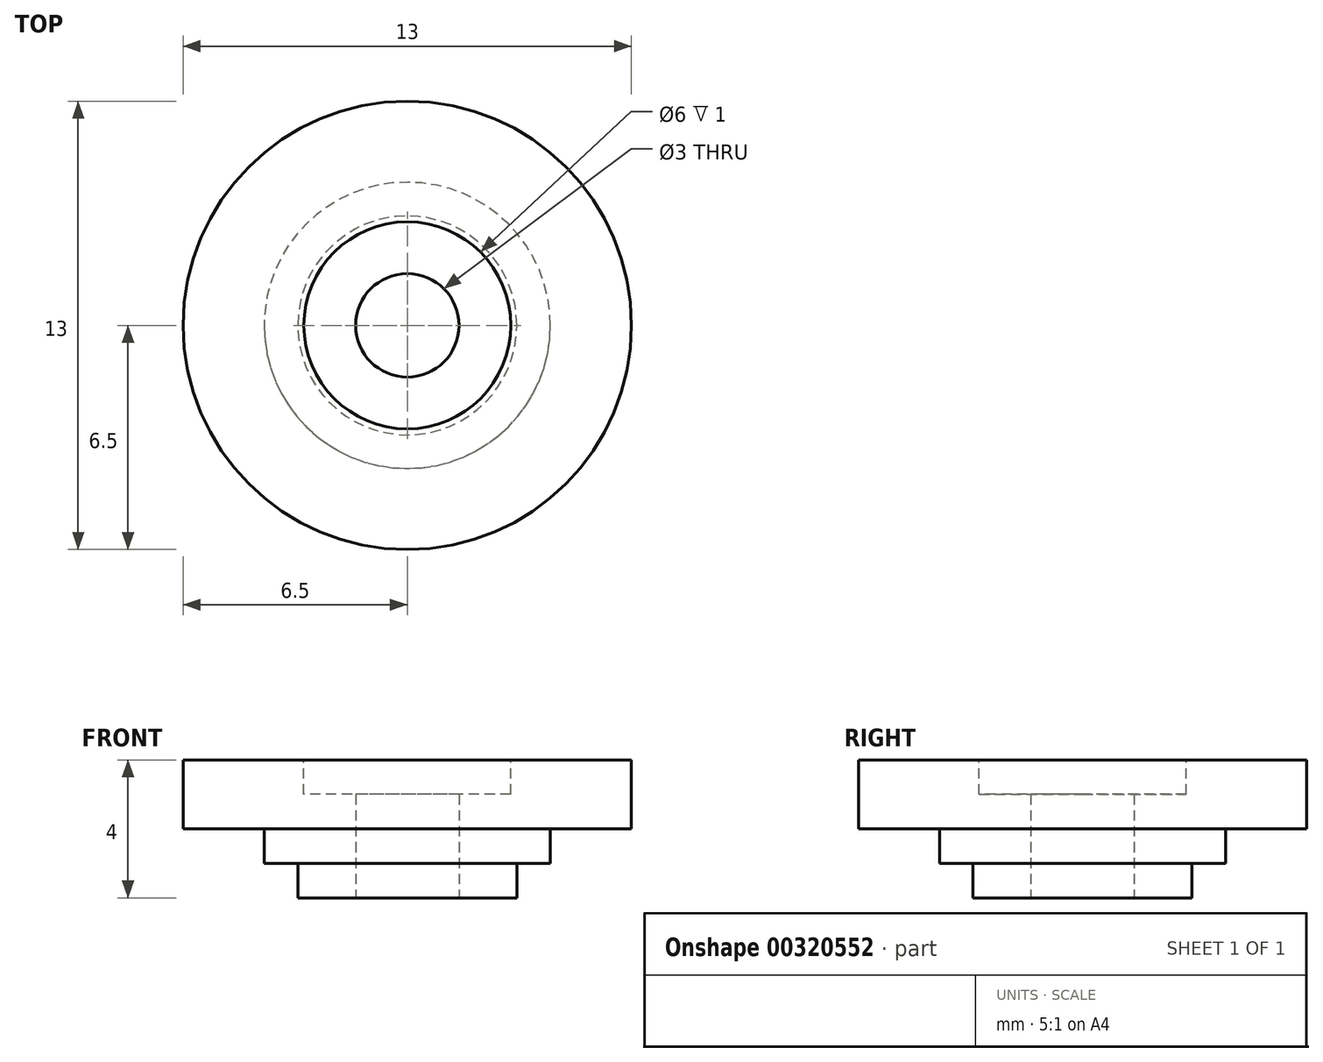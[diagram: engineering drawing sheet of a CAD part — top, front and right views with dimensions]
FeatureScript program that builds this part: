
annotation { "Feature Type Name" : "Feature", "Feature Type Description" : "" }
export const myFeature = defineFeature(function(context is Context, id is Id, definition is map)
    precondition{}
    {
        {
            var Q0;
            Q0=qCreatedBy(makeId("Top.planeOp"),FACE);
            var sketch = newSketch(context, id + "F0", { "sketchPlane" : qUnion([Q0])});
            skCircle(sketch, "E0", {"center": v(0, 0) * mm, "radius": 3.18 * mm});
            skSolve(sketch);
        }
        {
            var Q0;
            Q0=qSketchRegion(id+"F0",true);
            extrude(context, id + "F1", {"entities" : qUnion([Q0]), "depth" : 2 * mm});
        }
        {
            var Q0;
            Q0=makeQuery(id+"F1.opExtrude","CAP_FACE",FACE,{"disambiguationData":[OSD([sQuery(id+"F0.wireOp",EDGE,"E0")])],"isStart":false});
            var sketch = newSketch(context, id + "F2", { "sketchPlane" : qUnion([Q0])});
            skCircle(sketch, "E1", {"center": v(0, 0) * mm, "radius": 6.5 * mm});
            skSolve(sketch);
        }
        {
            var Q0;
            Q0=qSketchRegion(id+"F2",true);
            extrude(context, id + "F3", {"entities" : qUnion([Q0]), "operationType" : NewBodyOperationType.ADD, "depth" : 2 * mm});
        }
        {
            var Q0;
            Q0=makeQuery(id+"F3.opExtrude","CAP_FACE",FACE,{"disambiguationData":[OSD([sQuery(id+"F2.wireOp",EDGE,"E1")])],"isStart":false});
            var sketch = newSketch(context, id + "F4", { "sketchPlane" : qUnion([Q0])});
            skCircle(sketch, "E2", {"center": v(0, 0) * mm, "radius": 3 * mm});
            skSolve(sketch);
        }
        {
            var Q0;
            Q0=makeQuery(id+"F4.imprint","IMPRINT",FACE,{"disambiguationData":[TD([[makeQuery(id+"F4.imprint","IMPRINT",EDGE,{"derivedFrom":sQuery(id+"F4.wireOp",EDGE,"E2")}),1.0]])]});
            extrude(context, id + "F5", {"entities" : qUnion([Q0]), "operationType" : NewBodyOperationType.REMOVE, "oppositeDirection" : true, "depth" : 1 * mm});
        }
        {
            var Q0;
            Q0=makeQuery(id+"F1.opExtrude","CAP_FACE",FACE,{"disambiguationData":[OSD([sQuery(id+"F0.wireOp",EDGE,"E0")])],"isStart":true});
            var sketch = newSketch(context, id + "F6", { "sketchPlane" : qUnion([Q0])});
            skCircle(sketch, "E3", {"center": v(0, 0) * mm, "radius": 1.5 * mm});
            skSolve(sketch);
        }
        {
            var Q0;
            Q0=qSketchRegion(id+"F6",true);
            extrude(context, id + "F7", {"entities" : qUnion([Q0]), "operationType" : NewBodyOperationType.REMOVE, "oppositeDirection" : true, "depth" : 25 * mm});
        }
        {
            var Q0;
            Q0=makeQuery(id+"F3.opExtrude","CAP_FACE",FACE,{"disambiguationData":[OSD([sQuery(id+"F2.wireOp",EDGE,"E1")])],"isStart":true});
            var sketch = newSketch(context, id + "F8", { "sketchPlane" : qUnion([Q0])});
            skCircle(sketch, "E4", {"center": v(0, 0) * mm, "radius": 4.15 * mm});
            skCircle(sketch, "E5.0", {"center": v(0, 0) * mm, "radius": 3.18 * mm});
            skSolve(sketch);
        }
        {
            var Q0;
            Q0=qSketchRegion(id+"F8",true);
            extrude(context, id + "F9", {"entities" : qUnion([Q0]), "operationType" : NewBodyOperationType.ADD, "depth" : 1 * mm});
        }
    });
